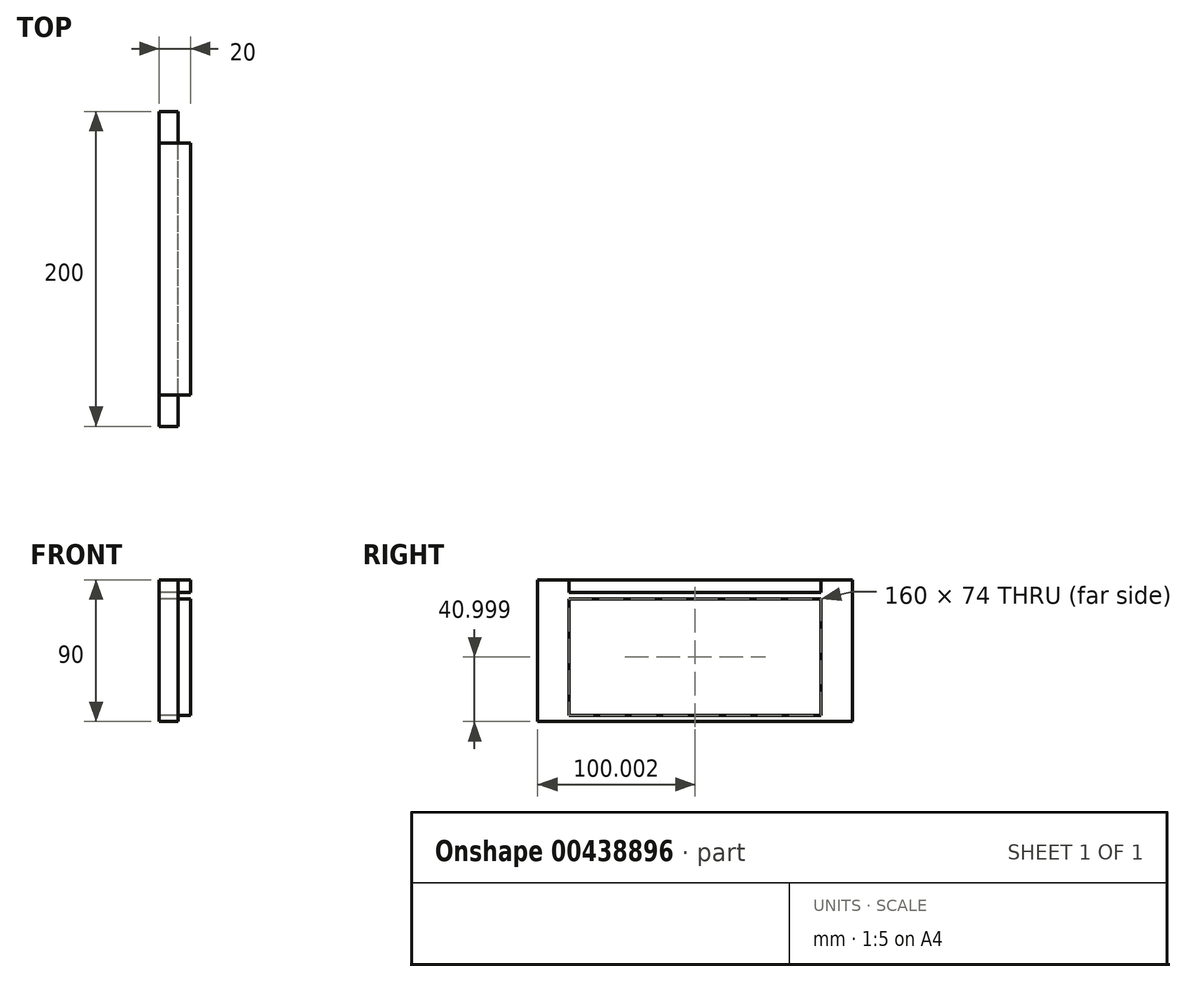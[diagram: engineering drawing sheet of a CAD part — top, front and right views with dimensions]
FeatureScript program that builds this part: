
annotation { "Feature Type Name" : "Feature", "Feature Type Description" : "" }
export const myFeature = defineFeature(function(context is Context, id is Id, definition is map)
    precondition{}
    {
        {
            var Q0;
            Q0=qCreatedBy(makeId("Right.planeOp"),FACE);
            var sketch = newSketch(context, id + "F0", { "sketchPlane" : qUnion([Q0])});
            skLineSegment(sketch, "E0", {"start": v(132.73, 42.28) * mm, "end": v(-67.27, 42.28) * mm});
            skLineSegment(sketch, "E1", {"start": v(-67.27, 42.28) * mm, "end": v(-67.27, -47.72) * mm});
            skLineSegment(sketch, "E2", {"start": v(-67.27, -47.72) * mm, "end": v(132.73, -47.72) * mm});
            skLineSegment(sketch, "E3", {"start": v(132.73, -47.72) * mm, "end": v(132.73, 42.28) * mm});
            skLineSegment(sketch, "E4", {"start": v(-47.27, 42.28) * mm, "end": v(-47.27, 34.28) * mm});
            skLineSegment(sketch, "E5", {"start": v(-47.27, 34.28) * mm, "end": v(112.73, 34.28) * mm});
            skLineSegment(sketch, "E6", {"start": v(112.73, 34.28) * mm, "end": v(112.73, 42.28) * mm});
            skLineSegment(sketch, "E7", {"start": v(112.73, 42.28) * mm, "end": v(-47.27, 42.28) * mm});
            skLineSegment(sketch, "E8.bottom", {"start": v(-47.27, 30.28) * mm, "end": v(112.73, 30.28) * mm});
            skLineSegment(sketch, "E8.top", {"start": v(-47.27, -43.72) * mm, "end": v(112.73, -43.72) * mm});
            skLineSegment(sketch, "E8.left", {"start": v(-47.27, 30.28) * mm, "end": v(-47.27, -43.72) * mm});
            skLineSegment(sketch, "E8.right", {"start": v(112.73, 30.28) * mm, "end": v(112.73, -43.72) * mm});
            skSolve(sketch);
        }
        {
            var Q0;
            Q0=makeQuery(id+"F0.imprint","IMPRINT",FACE,{"disambiguationData":[TD([[makeQuery(id+"F0.imprint","IMPRINT",EDGE,{"derivedFrom":sQuery(id+"F0.wireOp",EDGE,"E4")}),1.0]])]});
            var Q1;
            Q1=makeQuery(id+"F0.imprint","IMPRINT",FACE,{"disambiguationData":[TD([[makeQuery(id+"F0.imprint","IMPRINT",EDGE,{"derivedFrom":sQuery(id+"F0.wireOp",EDGE,"E8.bottom")}),-1.0]])]});
            extrude(context, id + "F1", {"entities" : qUnion([Q0, Q1]), "depth" : 20 * mm});
        }
        {
            var Q0;
            {var subQ5=sQuery(id+"F0.wireOp",EDGE,"E1");Q0=makeQuery(id+"F0.imprint","IMPRINT",FACE,{"disambiguationData":[TD([[makeQuery(id+"F0.imprint","IMPRINT",EDGE,{"derivedFrom":subQ5}),1.0]])]});}
            extrude(context, id + "F2", {"entities" : qUnion([Q0]), "depth" : 12 * mm});
        }
    });
